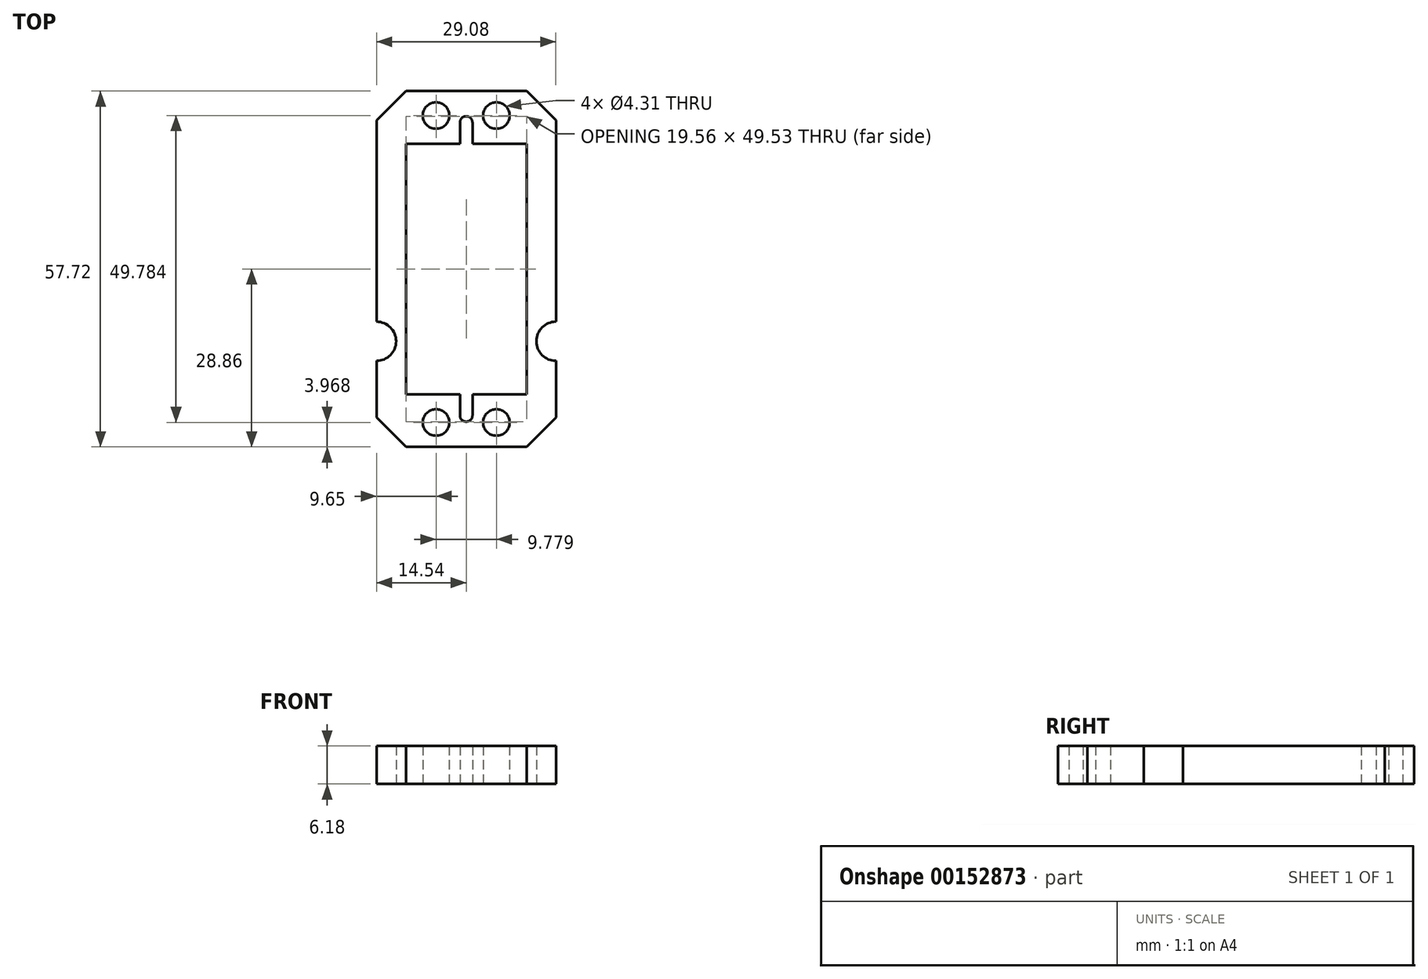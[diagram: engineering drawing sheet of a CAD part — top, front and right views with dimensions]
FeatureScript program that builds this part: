
annotation { "Feature Type Name" : "Feature", "Feature Type Description" : "" }
export const myFeature = defineFeature(function(context is Context, id is Id, definition is map)
    precondition{}
    {
        {
            var Q0;
            Q0=qCreatedBy(makeId("Top.planeOp"),FACE);
            var sketch = newSketch(context, id + "F0", { "sketchPlane" : qUnion([Q0])});
            skLineSegment(sketch, "E0.left", {"start": v(9.78, -20.32) * mm, "end": v(9.78, 20.32) * mm});
            skLineSegment(sketch, "E0.right", {"start": v(-9.78, -20.32) * mm, "end": v(-9.78, 20.32) * mm});
            skPoint(sketch, "E0.middle", {"position": v(0, 0) * mm});
            skLineSegment(sketch, "E1.bottom", {"start": v(4.89, 24.9) * mm, "end": v(-4.89, 24.9) * mm, "construction": true});
            skLineSegment(sketch, "E1.top", {"start": v(4.89, -24.9) * mm, "end": v(-4.89, -24.9) * mm, "construction": true});
            skLineSegment(sketch, "E1.left", {"start": v(4.89, 24.9) * mm, "end": v(4.89, -24.9) * mm, "construction": true});
            skLineSegment(sketch, "E1.right", {"start": v(-4.89, 24.9) * mm, "end": v(-4.89, -24.9) * mm, "construction": true});
            skCircle(sketch, "E2", {"center": v(-4.89, 24.9) * mm, "radius": 2.15 * mm});
            skCircle(sketch, "E3", {"center": v(-4.89, -24.9) * mm, "radius": 2.15 * mm});
            skCircle(sketch, "E4", {"center": v(4.89, -24.9) * mm, "radius": 2.15 * mm});
            skCircle(sketch, "E5", {"center": v(4.89, 24.9) * mm, "radius": 2.15 * mm});
            skLineSegment(sketch, "E6", {"start": v(14.54, 20.32) * mm, "end": v(14.54, -11.73) * mm, "construction": true});
            skLineSegment(sketch, "E7", {"start": v(9.78, 20.32) * mm, "end": v(14.54, 20.32) * mm, "construction": true});
            skLineSegment(sketch, "E8", {"start": v(-9.78, 20.32) * mm, "end": v(-14.54, 20.32) * mm, "construction": true});
            skLineSegment(sketch, "E9", {"start": v(-14.54, 20.32) * mm, "end": v(-14.54, -11.73) * mm, "construction": true});
            skLineSegment(sketch, "E10", {"start": v(9.78, 20.32) * mm, "end": v(1.02, 20.32) * mm});
            skLineSegment(sketch, "E11", {"start": v(-9.78, 20.32) * mm, "end": v(-1.02, 20.32) * mm});
            skLineSegment(sketch, "E12.bottom", {"start": v(1.02, 20.32) * mm, "end": v(-1.02, 20.32) * mm, "construction": true});
            skLineSegment(sketch, "E12.top", {"start": v(1.02, 23.75) * mm, "end": v(-1.02, 23.75) * mm, "construction": true});
            skLineSegment(sketch, "E12.left", {"start": v(1.02, 20.32) * mm, "end": v(1.02, 23.75) * mm});
            skLineSegment(sketch, "E12.right", {"start": v(-1.02, 20.32) * mm, "end": v(-1.02, 23.75) * mm});
            skLineSegment(sketch, "E13", {"start": v(9.78, -20.32) * mm, "end": v(1.02, -20.32) * mm});
            skLineSegment(sketch, "E14", {"start": v(-9.78, -20.32) * mm, "end": v(-1.02, -20.32) * mm});
            skLineSegment(sketch, "E15.bottom", {"start": v(1.02, -20.32) * mm, "end": v(-1.02, -20.32) * mm, "construction": true});
            skLineSegment(sketch, "E15.top", {"start": v(1.02, -23.75) * mm, "end": v(-1.02, -23.75) * mm, "construction": true});
            skLineSegment(sketch, "E15.left", {"start": v(1.02, -20.32) * mm, "end": v(1.02, -23.75) * mm});
            skLineSegment(sketch, "E15.right", {"start": v(-1.02, -20.32) * mm, "end": v(-1.02, -23.75) * mm});
            skArc(sketch, "E16", {"start": v(-1.02, -23.75) * mm, "mid": v(0, -24.77) * mm, "end": v(1.02, -23.75) * mm});
            skArc(sketch, "E17", {"start": v(1.02, 23.75) * mm, "mid": v(0, 24.77) * mm, "end": v(-1.02, 23.75) * mm});
            skArc(sketch, "E18", {"start": v(-14.54, -14.9) * mm, "mid": v(-11.37, -11.73) * mm, "end": v(-14.54, -8.55) * mm});
            skArc(sketch, "E19", {"start": v(14.54, -8.55) * mm, "mid": v(11.37, -11.73) * mm, "end": v(14.54, -14.9) * mm});
            skLineSegment(sketch, "E20", {"start": v(-14.54, -14.9) * mm, "end": v(-14.54, -28.86) * mm});
            skLineSegment(sketch, "E21", {"start": v(-14.54, -28.86) * mm, "end": v(14.54, -28.86) * mm});
            skLineSegment(sketch, "E22", {"start": v(14.54, -28.86) * mm, "end": v(14.54, -14.9) * mm});
            skLineSegment(sketch, "E23", {"start": v(0, -24.9) * mm, "end": v(0, -28.86) * mm, "construction": true});
            skLineSegment(sketch, "E24", {"start": v(9.78, 0) * mm, "end": v(14.54, 0) * mm, "construction": true});
            skLineSegment(sketch, "E25", {"start": v(14.54, -8.55) * mm, "end": v(14.54, 28.86) * mm});
            skLineSegment(sketch, "E26", {"start": v(14.54, 28.86) * mm, "end": v(-14.54, 28.86) * mm});
            skLineSegment(sketch, "E27", {"start": v(-14.54, 28.86) * mm, "end": v(-14.54, -8.55) * mm});
            skLineSegment(sketch, "E28", {"start": v(0, 24.9) * mm, "end": v(0, 28.86) * mm, "construction": true});
            skSolve(sketch);
        }
        {
            var Q0;
            Q0=qSketchRegion(id+"F0",true);
            extrude(context, id + "F1", {"entities" : qUnion([Q0]), "depth" : 6.18 * mm});
        }
        {
            var Q0;
            Q0=makeQuery(id+"F1.opExtrude","SWEPT_EDGE",EDGE,{"disambiguationData":[OSD([sQuery(id+"F0.wireOp",EDGE,"E21"),sQuery(id+"F0.wireOp",EDGE,"E22")])]});
            var Q1;
            Q1=makeQuery(id+"F1.opExtrude","SWEPT_EDGE",EDGE,{"disambiguationData":[OSD([sQuery(id+"F0.wireOp",EDGE,"E25"),sQuery(id+"F0.wireOp",EDGE,"E26")])]});
            var Q2;
            Q2=makeQuery(id+"F1.opExtrude","SWEPT_EDGE",EDGE,{"disambiguationData":[OSD([sQuery(id+"F0.wireOp",EDGE,"E26"),sQuery(id+"F0.wireOp",EDGE,"E27")])]});
            var Q3;
            Q3=makeQuery(id+"F1.opExtrude","SWEPT_EDGE",EDGE,{"disambiguationData":[OSD([sQuery(id+"F0.wireOp",EDGE,"E20"),sQuery(id+"F0.wireOp",EDGE,"E21")])]});
            chamfer(context, id + "F2", {"entities" : qUnion([Q0, Q1, Q2, Q3]), "width" : 4.76 * mm, "tangentPropagation" : true});
        }
    });
